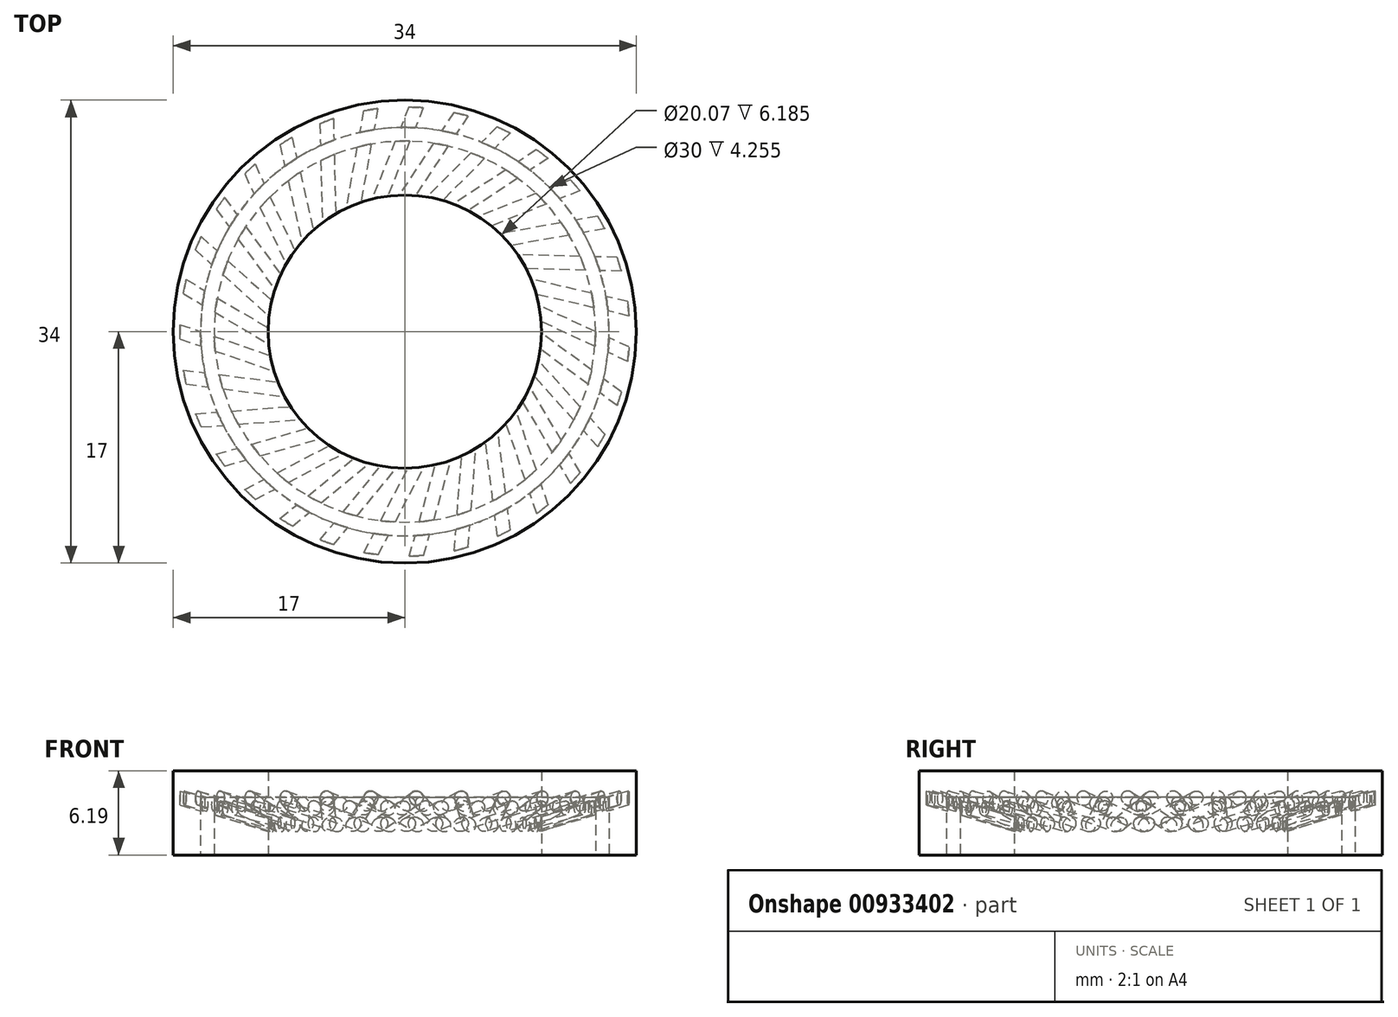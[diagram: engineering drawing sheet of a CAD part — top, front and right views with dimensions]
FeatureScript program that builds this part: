
annotation { "Feature Type Name" : "Feature", "Feature Type Description" : "" }
export const myFeature = defineFeature(function(context is Context, id is Id, definition is map)
    precondition{}
    {
        {
            var Q0;
            Q0=qCreatedBy(makeId("Top.planeOp"),FACE);
            var sketch = newSketch(context, id + "F0", { "sketchPlane" : qUnion([Q0])});
            skCircle(sketch, "E0", {"center": v(0, 0) * mm, "radius": 16.5 * mm});
            skSolve(sketch);
        }
        {
            var Q0;
            Q0=makeQuery(id+"F0.imprint","IMPRINT",FACE,{"disambiguationData":[TD([[makeQuery(id+"F0.imprint","IMPRINT",EDGE,{"derivedFrom":sQuery(id+"F0.wireOp",EDGE,"E0")}),1.0]])]});
            extrude(context, id + "F1", {"entities" : qUnion([Q0]), "depth" : 7.94 * mm, "offsetDistance" : 25.4 * mm});
        }
        {
            var Q0;
            Q0=qCreatedBy(makeId("Top.planeOp"),FACE);
            var sketch = newSketch(context, id + "F2", { "sketchPlane" : qUnion([Q0])});
            skCircle(sketch, "E1", {"center": v(0, 0) * mm, "radius": 10.03 * mm});
            skSolve(sketch);
        }
        {
            var Q0;
            Q0 = qSketchRegion(id + "F2", true);
            extrude(context, id + "F3", {"entities" : qUnion([Q0]), "operationType" : NewBodyOperationType.REMOVE, "depth" : 7.94 * mm, "offsetDistance" : 25.4 * mm});
        }
        {
            var Q0;
            Q0=qCreatedBy(makeId("Right.planeOp"),FACE);
            var sketch = newSketch(context, id + "F4", { "sketchPlane" : qUnion([Q0])});
            skLineSegment(sketch, "E2", {"start": v(0, 0) * mm, "end": v(0, 143.33) * mm});
            skLineSegment(sketch, "E3", {"start": v(-8.9, 0) * mm, "end": v(-8.9, 70.97) * mm});
            skSolve(sketch);
        }
        {
            var Q0;
            Q0=qCreatedBy(makeId("Top.planeOp"),FACE);
            var sketch = newSketch(context, id + "F5", { "sketchPlane" : qUnion([Q0])});
            skLineSegment(sketch, "E4", {"start": v(0, 0) * mm, "end": v(29.86, 0) * mm});
            skSolve(sketch);
        }
        {
            var Q0;
            Q0=qCreatedBy(makeId("Right.planeOp"),FACE);
            var sketch = newSketch(context, id + "F6", { "sketchPlane" : qUnion([Q0])});
            skCircle(sketch, "E5", {"center": v(0, 54.1) * mm, "radius": 0.5 * mm});
            skSolve(sketch);
        }
        {
            var Q0;
            Q0=makeQuery(id+"F6.imprint","IMPRINT",FACE,{"disambiguationData":[TD([[makeQuery(id+"F6.imprint","IMPRINT",EDGE,{"derivedFrom":sQuery(id+"F6.wireOp",EDGE,"E5")}),1.0]])]});
            extrude(context, id + "F7", {"entities" : qUnion([Q0]), "depth" : 25.4 * mm, "offsetDistance" : 25.4 * mm});
        }
        {
            var Q0;
            Q0=makeQuery(id+"F7.opExtrude","SWEPT_BODY",BODY,{"disambiguationData":[OSD([sQuery(id+"F6.wireOp",EDGE,"E5")])]});
            var Q1;
            Q1=sQuery(id+"F4.wireOp",EDGE,"E2");
            transform(context, id + "F8", {"entities" : qUnion([Q0]), "transformType" : TransformType.ROTATION, "transformAxis" : qUnion([Q1]), "angle" : 20 * degree, "makeCopy" : false});
        }
        {
            var Q0;
            Q0=makeQuery(id+"F7.opExtrude","SWEPT_BODY",BODY,{"disambiguationData":[OSD([sQuery(id+"F6.wireOp",EDGE,"E5")])]});
            transform(context, id + "F9", {"entities" : qUnion([Q0]), "transformType" : TransformType.TRANSLATION_3D, "dx" : 0 * mm, "dy" : 0 * mm, "dz" : -54.1 * mm, "makeCopy" : false});
        }
        {
            var Q0;
            Q0=makeQuery(id+"F7.opExtrude","SWEPT_BODY",BODY,{"disambiguationData":[OSD([sQuery(id+"F6.wireOp",EDGE,"E5")])]});
            var Q1;
            Q1=sQuery(id+"F5.wireOp",EDGE,"E4");
            var Q2;
            Q2=sQuery(id+"F5.wireOp",EDGE,"E4");
            transform(context, id + "F10", {"entities" : qUnion([Q0]), "transformType" : TransformType.ROTATION, "transformAxis" : qUnion([Q2]), "angle" : 50 * degree, "makeCopy" : false});
        }
        {
            var Q0;
            Q0=makeQuery(id+"F7.opExtrude","SWEPT_BODY",BODY,{"disambiguationData":[OSD([sQuery(id+"F6.wireOp",EDGE,"E5")])]});
            var Q1;
            Q1=sQuery(id+"F4.wireOp",EDGE,"E2");
            var Q2;
            Q2=sQuery(id+"F4.wireOp",EDGE,"E3");
            transform(context, id + "F11", {"entities" : qUnion([Q0]), "transformType" : TransformType.ROTATION, "transformAxis" : qUnion([Q2]), "angle" : 55 * degree, "makeCopy" : false});
        }
        {
            var Q0;
            Q0=makeQuery(id+"F7.opExtrude","SWEPT_BODY",BODY,{"disambiguationData":[OSD([sQuery(id+"F6.wireOp",EDGE,"E5")])]});
            var Q1;
            Q1=sQuery(id+"F4.wireOp",EDGE,"E2");
            circularPattern(context, id + "F12", {"entities" : qUnion([Q0]), "axis" : qUnion([Q1]), "angle" : 360 * degree, "instanceCount" : 31, "equalSpace" : true});
        }
        {
            var Q0;
            Q0=makeQuery(id+"F7.opExtrude","SWEPT_BODY",BODY,{"disambiguationData":[OSD([sQuery(id+"F6.wireOp",EDGE,"E5")])]});
            var Q1;
            Q1=makeQuery(id+"F12.opPattern","COPY",BODY,{"derivedFrom":makeQuery(id+"F7.opExtrude","SWEPT_BODY",BODY,{"disambiguationData":[OSD([sQuery(id+"F6.wireOp",EDGE,"E5")])]}),"instanceName":"14"});
            var Q2;
            Q2=makeQuery(id+"F1.opExtrude","SWEPT_BODY",BODY,{"disambiguationData":[OSD([sQuery(id+"F0.wireOp",EDGE,"E0")])]});
            booleanBodies(context, id + "F13", {"operationType" : BooleanOperationType.SUBTRACTION, "tools" : qUnion([Q0, Q1]), "targets" : qUnion([Q2])});
        }
        {
            var Q0;
            Q0=makeQuery(id+"F12.opPattern","COPY",BODY,{"derivedFrom":makeQuery(id+"F7.opExtrude","SWEPT_BODY",BODY,{"disambiguationData":[OSD([sQuery(id+"F6.wireOp",EDGE,"E5")])]}),"instanceName":"30"});
            var Q1;
            Q1=makeQuery(id+"F12.opPattern","COPY",BODY,{"derivedFrom":makeQuery(id+"F7.opExtrude","SWEPT_BODY",BODY,{"disambiguationData":[OSD([sQuery(id+"F6.wireOp",EDGE,"E5")])]}),"instanceName":"28"});
            var Q2;
            Q2=makeQuery(id+"F12.opPattern","COPY",BODY,{"derivedFrom":makeQuery(id+"F7.opExtrude","SWEPT_BODY",BODY,{"disambiguationData":[OSD([sQuery(id+"F6.wireOp",EDGE,"E5")])]}),"instanceName":"26"});
            var Q3;
            Q3=makeQuery(id+"F12.opPattern","COPY",BODY,{"derivedFrom":makeQuery(id+"F7.opExtrude","SWEPT_BODY",BODY,{"disambiguationData":[OSD([sQuery(id+"F6.wireOp",EDGE,"E5")])]}),"instanceName":"24"});
            var Q4;
            Q4=makeQuery(id+"F12.opPattern","COPY",BODY,{"derivedFrom":makeQuery(id+"F7.opExtrude","SWEPT_BODY",BODY,{"disambiguationData":[OSD([sQuery(id+"F6.wireOp",EDGE,"E5")])]}),"instanceName":"22"});
            var Q5;
            Q5=makeQuery(id+"F1.opExtrude","SWEPT_BODY",BODY,{"disambiguationData":[OSD([sQuery(id+"F0.wireOp",EDGE,"E0")])]});
            booleanBodies(context, id + "F14", {"operationType" : BooleanOperationType.SUBTRACTION, "tools" : qUnion([Q0, Q1, Q2, Q3, Q4]), "targets" : qUnion([Q5])});
        }
        {
            var Q0;
            Q0=makeQuery(id+"F12.opPattern","COPY",BODY,{"derivedFrom":makeQuery(id+"F7.opExtrude","SWEPT_BODY",BODY,{"disambiguationData":[OSD([sQuery(id+"F6.wireOp",EDGE,"E5")])]}),"instanceName":"20"});
            var Q1;
            Q1=makeQuery(id+"F12.opPattern","COPY",BODY,{"derivedFrom":makeQuery(id+"F7.opExtrude","SWEPT_BODY",BODY,{"disambiguationData":[OSD([sQuery(id+"F6.wireOp",EDGE,"E5")])]}),"instanceName":"18"});
            var Q2;
            Q2=makeQuery(id+"F12.opPattern","COPY",BODY,{"derivedFrom":makeQuery(id+"F7.opExtrude","SWEPT_BODY",BODY,{"disambiguationData":[OSD([sQuery(id+"F6.wireOp",EDGE,"E5")])]}),"instanceName":"16"});
            var Q3;
            Q3=makeQuery(id+"F12.opPattern","COPY",BODY,{"derivedFrom":makeQuery(id+"F7.opExtrude","SWEPT_BODY",BODY,{"disambiguationData":[OSD([sQuery(id+"F6.wireOp",EDGE,"E5")])]}),"instanceName":"13"});
            var Q4;
            Q4=makeQuery(id+"F12.opPattern","COPY",BODY,{"derivedFrom":makeQuery(id+"F7.opExtrude","SWEPT_BODY",BODY,{"disambiguationData":[OSD([sQuery(id+"F6.wireOp",EDGE,"E5")])]}),"instanceName":"11"});
            var Q5;
            Q5=makeQuery(id+"F12.opPattern","COPY",BODY,{"derivedFrom":makeQuery(id+"F7.opExtrude","SWEPT_BODY",BODY,{"disambiguationData":[OSD([sQuery(id+"F6.wireOp",EDGE,"E5")])]}),"instanceName":"9"});
            var Q6;
            Q6=makeQuery(id+"F12.opPattern","COPY",BODY,{"derivedFrom":makeQuery(id+"F7.opExtrude","SWEPT_BODY",BODY,{"disambiguationData":[OSD([sQuery(id+"F6.wireOp",EDGE,"E5")])]}),"instanceName":"7"});
            var Q7;
            Q7=makeQuery(id+"F12.opPattern","COPY",BODY,{"derivedFrom":makeQuery(id+"F7.opExtrude","SWEPT_BODY",BODY,{"disambiguationData":[OSD([sQuery(id+"F6.wireOp",EDGE,"E5")])]}),"instanceName":"5"});
            var Q8;
            Q8=makeQuery(id+"F12.opPattern","COPY",BODY,{"derivedFrom":makeQuery(id+"F7.opExtrude","SWEPT_BODY",BODY,{"disambiguationData":[OSD([sQuery(id+"F6.wireOp",EDGE,"E5")])]}),"instanceName":"3"});
            var Q9;
            Q9=makeQuery(id+"F12.opPattern","COPY",BODY,{"derivedFrom":makeQuery(id+"F7.opExtrude","SWEPT_BODY",BODY,{"disambiguationData":[OSD([sQuery(id+"F6.wireOp",EDGE,"E5")])]}),"instanceName":"1"});
            var Q10;
            Q10=makeQuery(id+"F1.opExtrude","SWEPT_BODY",BODY,{"disambiguationData":[OSD([sQuery(id+"F0.wireOp",EDGE,"E0")])]});
            booleanBodies(context, id + "F15", {"operationType" : BooleanOperationType.SUBTRACTION, "tools" : qUnion([Q0, Q1, Q2, Q3, Q4, Q5, Q6, Q7, Q8, Q9]), "targets" : qUnion([Q10])});
        }
        {
            var Q0;
            Q0=makeQuery(id+"F12.opPattern","COPY",BODY,{"derivedFrom":makeQuery(id+"F7.opExtrude","SWEPT_BODY",BODY,{"disambiguationData":[OSD([sQuery(id+"F6.wireOp",EDGE,"E5")])]}),"instanceName":"29"});
            var Q1;
            Q1=makeQuery(id+"F12.opPattern","COPY",BODY,{"derivedFrom":makeQuery(id+"F7.opExtrude","SWEPT_BODY",BODY,{"disambiguationData":[OSD([sQuery(id+"F6.wireOp",EDGE,"E5")])]}),"instanceName":"27"});
            var Q2;
            Q2=makeQuery(id+"F12.opPattern","COPY",BODY,{"derivedFrom":makeQuery(id+"F7.opExtrude","SWEPT_BODY",BODY,{"disambiguationData":[OSD([sQuery(id+"F6.wireOp",EDGE,"E5")])]}),"instanceName":"25"});
            var Q3;
            Q3=makeQuery(id+"F12.opPattern","COPY",BODY,{"derivedFrom":makeQuery(id+"F7.opExtrude","SWEPT_BODY",BODY,{"disambiguationData":[OSD([sQuery(id+"F6.wireOp",EDGE,"E5")])]}),"instanceName":"23"});
            var Q4;
            Q4=makeQuery(id+"F12.opPattern","COPY",BODY,{"derivedFrom":makeQuery(id+"F7.opExtrude","SWEPT_BODY",BODY,{"disambiguationData":[OSD([sQuery(id+"F6.wireOp",EDGE,"E5")])]}),"instanceName":"21"});
            var Q5;
            Q5=makeQuery(id+"F12.opPattern","COPY",BODY,{"derivedFrom":makeQuery(id+"F7.opExtrude","SWEPT_BODY",BODY,{"disambiguationData":[OSD([sQuery(id+"F6.wireOp",EDGE,"E5")])]}),"instanceName":"19"});
            var Q6;
            Q6=makeQuery(id+"F12.opPattern","COPY",BODY,{"derivedFrom":makeQuery(id+"F7.opExtrude","SWEPT_BODY",BODY,{"disambiguationData":[OSD([sQuery(id+"F6.wireOp",EDGE,"E5")])]}),"instanceName":"17"});
            var Q7;
            Q7=makeQuery(id+"F12.opPattern","COPY",BODY,{"derivedFrom":makeQuery(id+"F7.opExtrude","SWEPT_BODY",BODY,{"disambiguationData":[OSD([sQuery(id+"F6.wireOp",EDGE,"E5")])]}),"instanceName":"15"});
            var Q8;
            Q8=makeQuery(id+"F12.opPattern","COPY",BODY,{"derivedFrom":makeQuery(id+"F7.opExtrude","SWEPT_BODY",BODY,{"disambiguationData":[OSD([sQuery(id+"F6.wireOp",EDGE,"E5")])]}),"instanceName":"12"});
            var Q9;
            Q9=makeQuery(id+"F12.opPattern","COPY",BODY,{"derivedFrom":makeQuery(id+"F7.opExtrude","SWEPT_BODY",BODY,{"disambiguationData":[OSD([sQuery(id+"F6.wireOp",EDGE,"E5")])]}),"instanceName":"10"});
            var Q10;
            Q10=makeQuery(id+"F12.opPattern","COPY",BODY,{"derivedFrom":makeQuery(id+"F7.opExtrude","SWEPT_BODY",BODY,{"disambiguationData":[OSD([sQuery(id+"F6.wireOp",EDGE,"E5")])]}),"instanceName":"8"});
            var Q11;
            Q11=makeQuery(id+"F12.opPattern","COPY",BODY,{"derivedFrom":makeQuery(id+"F7.opExtrude","SWEPT_BODY",BODY,{"disambiguationData":[OSD([sQuery(id+"F6.wireOp",EDGE,"E5")])]}),"instanceName":"6"});
            var Q12;
            Q12=makeQuery(id+"F12.opPattern","COPY",BODY,{"derivedFrom":makeQuery(id+"F7.opExtrude","SWEPT_BODY",BODY,{"disambiguationData":[OSD([sQuery(id+"F6.wireOp",EDGE,"E5")])]}),"instanceName":"4"});
            var Q13;
            Q13=makeQuery(id+"F12.opPattern","COPY",BODY,{"derivedFrom":makeQuery(id+"F7.opExtrude","SWEPT_BODY",BODY,{"disambiguationData":[OSD([sQuery(id+"F6.wireOp",EDGE,"E5")])]}),"instanceName":"2"});
            var Q14;
            Q14=makeQuery(id+"F1.opExtrude","SWEPT_BODY",BODY,{"disambiguationData":[OSD([sQuery(id+"F0.wireOp",EDGE,"E0")])]});
            booleanBodies(context, id + "F16", {"operationType" : BooleanOperationType.SUBTRACTION, "tools" : qUnion([Q0, Q1, Q2, Q3, Q4, Q5, Q6, Q7, Q8, Q9, Q10, Q11, Q12, Q13]), "targets" : qUnion([Q14])});
        }
        {
            var Q0;
            Q0=makeQuery(id+"F1.opExtrude","CAP_FACE",FACE,{"disambiguationData":[OSD([sQuery(id+"F0.wireOp",EDGE,"E0")])],"isStart":true});
            var sketch = newSketch(context, id + "F17", { "sketchPlane" : qUnion([Q0])});
            skCircle(sketch, "E6", {"center": v(0, 0) * mm, "radius": 16.5 * mm});
            skSolve(sketch);
        }
        {
            var Q0;
            Q0=makeQuery(id+"F17.imprint","IMPRINT",FACE,{"disambiguationData":[TD([[makeQuery(id+"F17.imprint","IMPRINT",EDGE,{"derivedFrom":sQuery(id+"F17.wireOp",EDGE,"E6")}),-1.0]])]});
            extrude(context, id + "F18", {"entities" : qUnion([Q0]), "operationType" : NewBodyOperationType.REMOVE, "oppositeDirection" : true, "depth" : 1.75 * mm, "offsetDistance" : 25.4 * mm});
        }
        {
            var Q0;
            Q0=makeQuery(id+"F18.boolean.opBoolean","COPY",FACE,{"derivedFrom":makeQuery(id+"F18.opExtrude","CAP_FACE",FACE,{"disambiguationData":[OSD([sQuery(id+"F2.wireOp",EDGE,"E1"),sQuery(id+"F17.wireOp",EDGE,"E6")])],"isStart":false})});
            var sketch = newSketch(context, id + "F19", { "sketchPlane" : qUnion([Q0])});
            skCircle(sketch, "E7", {"center": v(0, 0) * mm, "radius": 15 * mm});
            skCircle(sketch, "E8", {"center": v(0, 0) * mm, "radius": 14 * mm});
            skSolve(sketch);
        }
        {
            var Q0;
            Q0=makeQuery(id+"F19.imprint","IMPRINT",FACE,{"disambiguationData":[TD([[makeQuery(id+"F19.imprint","IMPRINT",EDGE,{"derivedFrom":sQuery(id+"F19.wireOp",EDGE,"E7")}),1.0]])]});
            var Q1;
            Q1=sQuery(id+"F19.wireOp",EDGE,"E7");
            var Q2;
            Q2=sQuery(id+"F19.wireOp",EDGE,"E8");
            var Q3;
            Q3=makeQuery(id+"F18.boolean.opBoolean","COPY",FACE,{"derivedFrom":makeQuery(id+"F18.opExtrude","CAP_FACE",FACE,{"disambiguationData":[OSD([sQuery(id+"F2.wireOp",EDGE,"E1"),sQuery(id+"F17.wireOp",EDGE,"E6")])],"isStart":false})});
            extrude(context, id + "F20", {"entities" : qUnion([Q0]), "operationType" : NewBodyOperationType.REMOVE, "surfaceEntities" : qUnion([Q1, Q2]), "oppositeDirection" : true, "depth" : 4.25 * mm, "endBoundEntityFace" : qUnion([Q3]), "offsetDistance" : 12.7 * mm, "offsetOppositeDirection" : true});
        }
        {
            var Q0;
            {var subQ0=sQuery(id+"F0.wireOp",EDGE,"E0");Q0=makeQuery(id+"F20.boolean.opBoolean","SPLIT",FACE,{"disambiguationData":[TD([makeQuery(id+"F1.opExtrude","SWEPT_FACE",FACE,{"disambiguationData":[OSD([subQ0])]})])],"derivedFrom":makeQuery(id+"F1.opExtrude","CAP_FACE",FACE,{"disambiguationData":[OSD([subQ0])],"isStart":false})});}
            var sketch = newSketch(context, id + "F21", { "sketchPlane" : qUnion([Q0])});
            skCircle(sketch, "E9", {"center": v(0, 0) * mm, "radius": 17 * mm});
            skSolve(sketch);
        }
        {
            var Q0;
            Q0=makeQuery(id+"F21.imprint","IMPRINT",FACE,{"disambiguationData":[TD([[makeQuery(id+"F21.imprint","IMPRINT",EDGE,{"derivedFrom":sQuery(id+"F21.wireOp",EDGE,"E9")}),1.0]])]});
            var Q1;
            Q1=makeQuery(id+"F18.boolean.opBoolean","COPY",FACE,{"derivedFrom":makeQuery(id+"F18.opExtrude","CAP_FACE",FACE,{"disambiguationData":[OSD([sQuery(id+"F2.wireOp",EDGE,"E1"),sQuery(id+"F17.wireOp",EDGE,"E6")])],"isStart":false})});
            var Q2;
            Q2=makeQuery(id+"F1.opExtrude","SWEPT_BODY",BODY,{"disambiguationData":[OSD([sQuery(id+"F0.wireOp",EDGE,"E0")])]});
            extrude(context, id + "F22", {"entities" : qUnion([Q0]), "operationType" : NewBodyOperationType.ADD, "endBound" : BoundingType.UP_TO_SURFACE, "oppositeDirection" : true, "depth" : 4.7 * mm, "endBoundEntityFace" : qUnion([Q1]), "endBoundEntityBody" : qUnion([Q2]), "offsetDistance" : 25.4 * mm});
        }
    });
